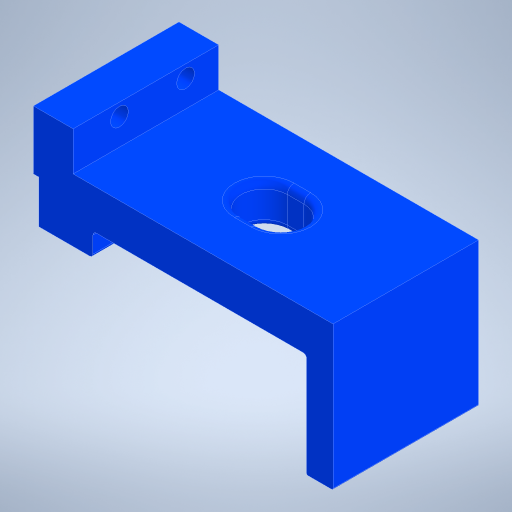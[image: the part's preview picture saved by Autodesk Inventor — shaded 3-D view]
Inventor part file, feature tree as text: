
AUTODESK INVENTOR PART (.ipt)
format: ipt  version: 2023.4 (Build 274418000, 418)  size: 357,376 bytes
history: native  units: in
note: dims shown in document units (in); Inventor stores cm internally (conversion verified against a paired STEP export)
features: sketch x6, extrude x3, fillet x3, other x1, hole x1
ambient origin geometry x8: Origin, YZ Plane, XZ Plane, XY Plane, X Axis, Y Axis, Z Axis, Center Point
bodies: Solid1 (feature_tree)
feature tree (14):
  other  "main_manifold_8v_v02.ipt"
  sketch  "Sketch: reference"  dims[d319=0.3in d1=1.5748in]
  sketch  "Sketch: side profile"  dims[d3=0.3in d5=0.095in]
  sketch  "Sketch: MM holes"  dims[d6=0.3in d7=0.0in]
  extrude  "Ex: MM screws"  TaperAngle=0.0deg  [1 undecoded]
  hole  "Hole: MM screws (4-40)"  [1 undecoded]
  extrude  "Ex: side profile"  Depth=0.3in
  sketch  "Sketch: center hole"  dims[d8=0.135in d9=0.75in d10=0.375in d11=0.25in d12=0.5635in d13=1.0in d14=0.8108in d21=0.295in d22=0.04in d23=1.0in d24=0.0in d25=0.175in]
  extrude  "Ex: center hole"  Depth=0.295in
  fillet  "Fillet1"  Radius=0.04in
  fillet  "Fillet2"  Radius=1.0in
  fillet  "Fillet3"  Radius=0.175in
  sketch  "Sketch:MM: main inlet"  dims[d30=0.05in d34=0.47in d43=0.15in d45=0.018in d47=0.89in d48=0.085in d49=0.18in d50=0.04in d51=0.3337in d52=0.15in d53=2.125in d54=0.025in d55=0.01in d56=0.475in d58=0.175in d59=0.0in d60=0.0in d61=0.05in d62=0.125in d63=0.475in d64=0.41in d65=0.45in d67=0.2in d68=0.7874in d69=0.0in d17=0.5in d18=0.0344in d19=0.5in d20=0.0344in]
  sketch  "Sketch:MM: mounting screws:1"  dims[d0=0.3937in d439=0.0in]
note: 2 required parameter values undecoded (feature->parameter linkage not recoverable at this tier; creation-order binding heuristic only, values carry confidence <= 0.55)
